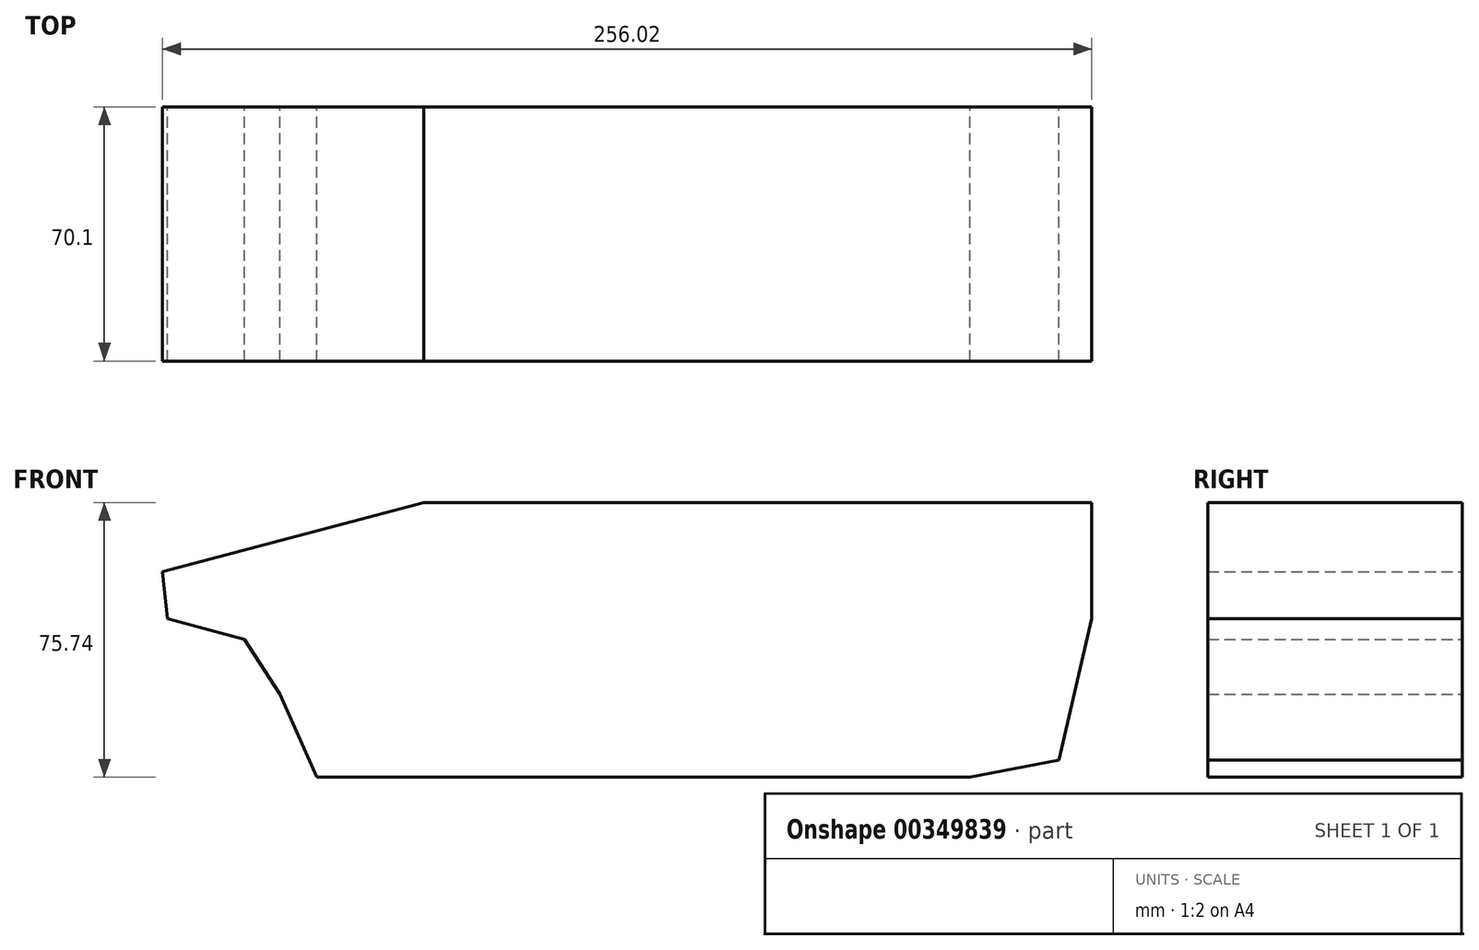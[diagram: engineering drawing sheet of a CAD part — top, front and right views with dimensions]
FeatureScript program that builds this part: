
annotation { "Feature Type Name" : "Feature", "Feature Type Description" : "" }
export const myFeature = defineFeature(function(context is Context, id is Id, definition is map)
    precondition{}
    {
        {
            var Q0;
            Q0=qCreatedBy(makeId("Front.planeOp"),FACE);
            var sketch = newSketch(context, id + "F0", { "sketchPlane" : qUnion([Q0])});
            skLineSegment(sketch, "E0", {"start": v(-104.19, 122.5) * mm, "end": v(79.81, 122.5) * mm});
            skLineSegment(sketch, "E1", {"start": v(79.81, 122.5) * mm, "end": v(79.81, 90.5) * mm});
            skLineSegment(sketch, "E2", {"start": v(79.81, 90.5) * mm, "end": v(70.81, 51.52) * mm});
            skLineSegment(sketch, "E3", {"start": v(70.81, 51.52) * mm, "end": v(46.27, 46.75) * mm});
            skLineSegment(sketch, "E4", {"start": v(46.27, 46.75) * mm, "end": v(-133.73, 46.75) * mm});
            skLineSegment(sketch, "E5", {"start": v(-133.73, 46.75) * mm, "end": v(-143.9, 69.59) * mm});
            skLineSegment(sketch, "E6", {"start": v(-143.9, 69.59) * mm, "end": v(-153.62, 84.73) * mm});
            skLineSegment(sketch, "E7", {"start": v(-153.62, 84.73) * mm, "end": v(-174.85, 90.5) * mm});
            skLineSegment(sketch, "E8", {"start": v(-174.85, 90.5) * mm, "end": v(-176.2, 103.43) * mm});
            skLineSegment(sketch, "E9", {"start": v(-176.2, 103.43) * mm, "end": v(-104.19, 122.5) * mm});
            skSolve(sketch);
        }
        {
            var Q0;
            Q0=makeQuery(id+"F0.imprint","IMPRINT",FACE,{"disambiguationData":[TD([[makeQuery(id+"F0.imprint","IMPRINT",EDGE,{"derivedFrom":sQuery(id+"F0.wireOp",EDGE,"E0")}),-1.0]])]});
            extrude(context, id + "F1", {"entities" : qUnion([Q0]), "endBound" : BoundingType.SYMMETRIC, "depth" : 70.1 * mm});
        }
    });
